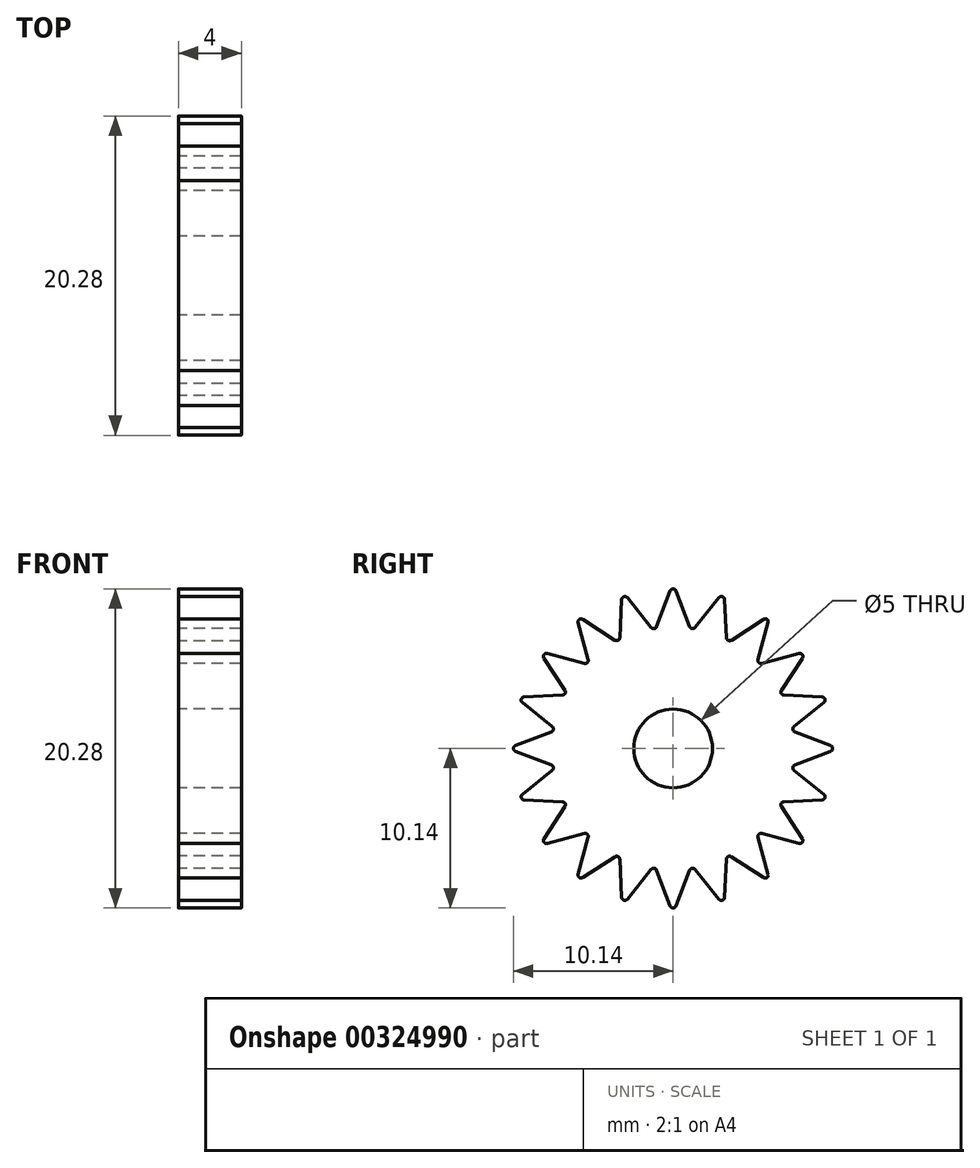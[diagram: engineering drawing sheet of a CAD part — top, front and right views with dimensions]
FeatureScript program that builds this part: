
annotation { "Feature Type Name" : "Feature", "Feature Type Description" : "" }
export const myFeature = defineFeature(function(context is Context, id is Id, definition is map)
    precondition{}
    {
        {
            var Q0;
            Q0=qCreatedBy(makeId("Right.planeOp"),FACE);
            var sketch = newSketch(context, id + "F0", { "sketchPlane" : qUnion([Q0])});
            skCircle(sketch, "E0", {"center": v(0, 0) * mm, "radius": 7.5 * mm, "construction": true});
            skLineSegment(sketch, "E1", {"start": v(-0.19, 10) * mm, "end": v(-1.05, 7.73) * mm});
            skLineSegment(sketch, "E2.MirrorCS", {"start": v(0.19, 10) * mm, "end": v(1.05, 7.73) * mm});
            skPoint(sketch, "E3.visualSharp", {"position": v(0, 10.5) * mm});
            skArc(sketch, "E3.filletArc", {"start": v(0.19, 10) * mm, "mid": v(0, 10.14) * mm, "end": v(-0.19, 10) * mm});
            skLineSegment(sketch, "E4.1.0", {"start": v(-3.27, 9.46) * mm, "end": v(-3.39, 7.03) * mm});
            skLineSegment(sketch, "E4.1.1", {"start": v(-2.91, 9.58) * mm, "end": v(-1.4, 7.68) * mm});
            skPoint(sketch, "E4.1.2", {"position": v(-3.24, 9.99) * mm});
            skArc(sketch, "E4.1.3", {"start": v(-2.91, 9.58) * mm, "mid": v(-3.13, 9.64) * mm, "end": v(-3.27, 9.46) * mm});
            skLineSegment(sketch, "E4.2.0", {"start": v(-6.03, 7.99) * mm, "end": v(-5.4, 5.64) * mm});
            skLineSegment(sketch, "E4.2.1", {"start": v(-5.73, 8.2) * mm, "end": v(-3.7, 6.87) * mm});
            skPoint(sketch, "E4.2.2", {"position": v(-6.17, 8.5) * mm});
            skArc(sketch, "E4.2.3", {"start": v(-5.73, 8.2) * mm, "mid": v(-5.96, 8.2) * mm, "end": v(-6.03, 7.99) * mm});
            skLineSegment(sketch, "E4.3.0", {"start": v(-8.2, 5.73) * mm, "end": v(-6.87, 3.7) * mm});
            skLineSegment(sketch, "E4.3.1", {"start": v(-7.99, 6.03) * mm, "end": v(-5.64, 5.4) * mm});
            skPoint(sketch, "E4.3.2", {"position": v(-8.5, 6.17) * mm});
            skArc(sketch, "E4.3.3", {"start": v(-7.99, 6.03) * mm, "mid": v(-8.2, 5.96) * mm, "end": v(-8.2, 5.73) * mm});
            skLineSegment(sketch, "E4.4.0", {"start": v(-9.58, 2.91) * mm, "end": v(-7.68, 1.4) * mm});
            skLineSegment(sketch, "E4.4.1", {"start": v(-9.46, 3.27) * mm, "end": v(-7.03, 3.39) * mm});
            skPoint(sketch, "E4.4.2", {"position": v(-9.99, 3.24) * mm});
            skArc(sketch, "E4.4.3", {"start": v(-9.46, 3.27) * mm, "mid": v(-9.64, 3.13) * mm, "end": v(-9.58, 2.91) * mm});
            skLineSegment(sketch, "E4.5.0", {"start": v(-10, -0.19) * mm, "end": v(-7.73, -1.05) * mm});
            skLineSegment(sketch, "E4.5.1", {"start": v(-10, 0.19) * mm, "end": v(-7.73, 1.05) * mm});
            skPoint(sketch, "E4.5.2", {"position": v(-10.5, 0) * mm});
            skArc(sketch, "E4.5.3", {"start": v(-10, 0.19) * mm, "mid": v(-10.14, 0) * mm, "end": v(-10, -0.19) * mm});
            skLineSegment(sketch, "E4.6.0", {"start": v(-9.46, -3.27) * mm, "end": v(-7.03, -3.39) * mm});
            skLineSegment(sketch, "E4.6.1", {"start": v(-9.58, -2.91) * mm, "end": v(-7.68, -1.4) * mm});
            skPoint(sketch, "E4.6.2", {"position": v(-9.99, -3.24) * mm});
            skArc(sketch, "E4.6.3", {"start": v(-9.58, -2.91) * mm, "mid": v(-9.64, -3.13) * mm, "end": v(-9.46, -3.27) * mm});
            skLineSegment(sketch, "E4.7.0", {"start": v(-7.99, -6.03) * mm, "end": v(-5.64, -5.4) * mm});
            skLineSegment(sketch, "E4.7.1", {"start": v(-8.2, -5.73) * mm, "end": v(-6.87, -3.7) * mm});
            skPoint(sketch, "E4.7.2", {"position": v(-8.5, -6.17) * mm});
            skArc(sketch, "E4.7.3", {"start": v(-8.2, -5.73) * mm, "mid": v(-8.2, -5.96) * mm, "end": v(-7.99, -6.03) * mm});
            skLineSegment(sketch, "E4.8.0", {"start": v(-5.73, -8.2) * mm, "end": v(-3.7, -6.87) * mm});
            skLineSegment(sketch, "E4.8.1", {"start": v(-6.03, -7.99) * mm, "end": v(-5.4, -5.64) * mm});
            skPoint(sketch, "E4.8.2", {"position": v(-6.17, -8.5) * mm});
            skArc(sketch, "E4.8.3", {"start": v(-6.03, -7.99) * mm, "mid": v(-5.96, -8.2) * mm, "end": v(-5.73, -8.2) * mm});
            skLineSegment(sketch, "E4.9.0", {"start": v(-2.91, -9.58) * mm, "end": v(-1.4, -7.68) * mm});
            skLineSegment(sketch, "E4.9.1", {"start": v(-3.27, -9.46) * mm, "end": v(-3.39, -7.03) * mm});
            skPoint(sketch, "E4.9.2", {"position": v(-3.24, -9.99) * mm});
            skArc(sketch, "E4.9.3", {"start": v(-3.27, -9.46) * mm, "mid": v(-3.13, -9.64) * mm, "end": v(-2.91, -9.58) * mm});
            skLineSegment(sketch, "E4.10.0", {"start": v(0.19, -10) * mm, "end": v(1.05, -7.73) * mm});
            skLineSegment(sketch, "E4.10.1", {"start": v(-0.19, -10) * mm, "end": v(-1.05, -7.73) * mm});
            skPoint(sketch, "E4.10.2", {"position": v(0, -10.5) * mm});
            skArc(sketch, "E4.10.3", {"start": v(-0.19, -10) * mm, "mid": v(0, -10.14) * mm, "end": v(0.19, -10) * mm});
            skLineSegment(sketch, "E4.11.0", {"start": v(3.27, -9.46) * mm, "end": v(3.39, -7.03) * mm});
            skLineSegment(sketch, "E4.11.1", {"start": v(2.91, -9.58) * mm, "end": v(1.4, -7.68) * mm});
            skPoint(sketch, "E4.11.2", {"position": v(3.24, -9.99) * mm});
            skArc(sketch, "E4.11.3", {"start": v(2.91, -9.58) * mm, "mid": v(3.13, -9.64) * mm, "end": v(3.27, -9.46) * mm});
            skLineSegment(sketch, "E4.12.0", {"start": v(6.03, -7.99) * mm, "end": v(5.4, -5.64) * mm});
            skLineSegment(sketch, "E4.12.1", {"start": v(5.73, -8.2) * mm, "end": v(3.7, -6.87) * mm});
            skPoint(sketch, "E4.12.2", {"position": v(6.17, -8.5) * mm});
            skArc(sketch, "E4.12.3", {"start": v(5.73, -8.2) * mm, "mid": v(5.96, -8.2) * mm, "end": v(6.03, -7.99) * mm});
            skLineSegment(sketch, "E4.13.0", {"start": v(8.2, -5.73) * mm, "end": v(6.87, -3.7) * mm});
            skLineSegment(sketch, "E4.13.1", {"start": v(7.99, -6.03) * mm, "end": v(5.64, -5.4) * mm});
            skPoint(sketch, "E4.13.2", {"position": v(8.5, -6.17) * mm});
            skArc(sketch, "E4.13.3", {"start": v(7.99, -6.03) * mm, "mid": v(8.2, -5.96) * mm, "end": v(8.2, -5.73) * mm});
            skLineSegment(sketch, "E4.14.0", {"start": v(9.58, -2.91) * mm, "end": v(7.68, -1.4) * mm});
            skLineSegment(sketch, "E4.14.1", {"start": v(9.46, -3.27) * mm, "end": v(7.03, -3.39) * mm});
            skPoint(sketch, "E4.14.2", {"position": v(9.99, -3.24) * mm});
            skArc(sketch, "E4.14.3", {"start": v(9.46, -3.27) * mm, "mid": v(9.64, -3.13) * mm, "end": v(9.58, -2.91) * mm});
            skLineSegment(sketch, "E4.15.0", {"start": v(10, 0.19) * mm, "end": v(7.73, 1.05) * mm});
            skLineSegment(sketch, "E4.15.1", {"start": v(10, -0.19) * mm, "end": v(7.73, -1.05) * mm});
            skPoint(sketch, "E4.15.2", {"position": v(10.5, 0) * mm});
            skArc(sketch, "E4.15.3", {"start": v(10, -0.19) * mm, "mid": v(10.14, 0) * mm, "end": v(10, 0.19) * mm});
            skLineSegment(sketch, "E4.16.0", {"start": v(9.46, 3.27) * mm, "end": v(7.03, 3.39) * mm});
            skLineSegment(sketch, "E4.16.1", {"start": v(9.58, 2.91) * mm, "end": v(7.68, 1.4) * mm});
            skPoint(sketch, "E4.16.2", {"position": v(9.99, 3.24) * mm});
            skArc(sketch, "E4.16.3", {"start": v(9.58, 2.91) * mm, "mid": v(9.64, 3.13) * mm, "end": v(9.46, 3.27) * mm});
            skLineSegment(sketch, "E4.17.0", {"start": v(7.99, 6.03) * mm, "end": v(5.64, 5.4) * mm});
            skLineSegment(sketch, "E4.17.1", {"start": v(8.2, 5.73) * mm, "end": v(6.87, 3.7) * mm});
            skPoint(sketch, "E4.17.2", {"position": v(8.5, 6.17) * mm});
            skArc(sketch, "E4.17.3", {"start": v(8.2, 5.73) * mm, "mid": v(8.2, 5.96) * mm, "end": v(7.99, 6.03) * mm});
            skLineSegment(sketch, "E4.18.0", {"start": v(5.73, 8.2) * mm, "end": v(3.7, 6.87) * mm});
            skLineSegment(sketch, "E4.18.1", {"start": v(6.03, 7.99) * mm, "end": v(5.4, 5.64) * mm});
            skPoint(sketch, "E4.18.2", {"position": v(6.17, 8.5) * mm});
            skArc(sketch, "E4.18.3", {"start": v(6.03, 7.99) * mm, "mid": v(5.96, 8.2) * mm, "end": v(5.73, 8.2) * mm});
            skLineSegment(sketch, "E4.19.0", {"start": v(2.91, 9.58) * mm, "end": v(1.4, 7.68) * mm});
            skLineSegment(sketch, "E4.19.1", {"start": v(3.27, 9.46) * mm, "end": v(3.39, 7.03) * mm});
            skPoint(sketch, "E4.19.2", {"position": v(3.24, 9.99) * mm});
            skArc(sketch, "E4.19.3", {"start": v(3.27, 9.46) * mm, "mid": v(3.13, 9.64) * mm, "end": v(2.91, 9.58) * mm});
            skPoint(sketch, "E5.visualSharp", {"position": v(1.17, 7.4) * mm});
            skArc(sketch, "E5.filletArc", {"start": v(1.05, 7.73) * mm, "mid": v(1.2, 7.6) * mm, "end": v(1.4, 7.68) * mm});
            skPoint(sketch, "E6.visualSharp", {"position": v(3.4, 6.68) * mm});
            skArc(sketch, "E6.filletArc", {"start": v(3.39, 7.03) * mm, "mid": v(3.5, 6.86) * mm, "end": v(3.7, 6.87) * mm});
            skPoint(sketch, "E7.visualSharp", {"position": v(5.3, 5.3) * mm});
            skArc(sketch, "E7.filletArc", {"start": v(5.4, 5.64) * mm, "mid": v(5.45, 5.45) * mm, "end": v(5.64, 5.4) * mm});
            skPoint(sketch, "E8.visualSharp", {"position": v(6.68, 3.4) * mm});
            skArc(sketch, "E8.filletArc", {"start": v(6.87, 3.7) * mm, "mid": v(6.86, 3.5) * mm, "end": v(7.03, 3.39) * mm});
            skPoint(sketch, "E9.visualSharp", {"position": v(7.4, 1.17) * mm});
            skArc(sketch, "E9.filletArc", {"start": v(7.68, 1.4) * mm, "mid": v(7.6, 1.2) * mm, "end": v(7.73, 1.05) * mm});
            skPoint(sketch, "E10.visualSharp", {"position": v(7.4, -1.17) * mm});
            skArc(sketch, "E10.filletArc", {"start": v(7.73, -1.05) * mm, "mid": v(7.6, -1.2) * mm, "end": v(7.68, -1.4) * mm});
            skPoint(sketch, "E11.visualSharp", {"position": v(-1.17, 7.4) * mm});
            skArc(sketch, "E11.filletArc", {"start": v(-1.4, 7.68) * mm, "mid": v(-1.2, 7.6) * mm, "end": v(-1.05, 7.73) * mm});
            skPoint(sketch, "E12.visualSharp", {"position": v(-3.4, 6.68) * mm});
            skArc(sketch, "E12.filletArc", {"start": v(-3.7, 6.87) * mm, "mid": v(-3.5, 6.86) * mm, "end": v(-3.39, 7.03) * mm});
            skPoint(sketch, "E13.visualSharp", {"position": v(-5.3, 5.3) * mm});
            skArc(sketch, "E13.filletArc", {"start": v(-5.64, 5.4) * mm, "mid": v(-5.45, 5.45) * mm, "end": v(-5.4, 5.64) * mm});
            skPoint(sketch, "E14.visualSharp", {"position": v(-6.68, 3.4) * mm});
            skArc(sketch, "E14.filletArc", {"start": v(-7.03, 3.39) * mm, "mid": v(-6.86, 3.5) * mm, "end": v(-6.87, 3.7) * mm});
            skPoint(sketch, "E15.visualSharp", {"position": v(-7.4, 1.17) * mm});
            skArc(sketch, "E15.filletArc", {"start": v(-7.73, 1.05) * mm, "mid": v(-7.6, 1.2) * mm, "end": v(-7.68, 1.4) * mm});
            skPoint(sketch, "E16.visualSharp", {"position": v(-7.4, -1.17) * mm});
            skArc(sketch, "E16.filletArc", {"start": v(-7.68, -1.4) * mm, "mid": v(-7.6, -1.2) * mm, "end": v(-7.73, -1.05) * mm});
            skPoint(sketch, "E17.visualSharp", {"position": v(-6.68, -3.4) * mm});
            skArc(sketch, "E17.filletArc", {"start": v(-6.87, -3.7) * mm, "mid": v(-6.86, -3.5) * mm, "end": v(-7.03, -3.39) * mm});
            skPoint(sketch, "E18.visualSharp", {"position": v(-5.3, -5.3) * mm});
            skArc(sketch, "E18.filletArc", {"start": v(-5.4, -5.64) * mm, "mid": v(-5.45, -5.45) * mm, "end": v(-5.64, -5.4) * mm});
            skPoint(sketch, "E19.visualSharp", {"position": v(-3.4, -6.68) * mm});
            skArc(sketch, "E19.filletArc", {"start": v(-3.39, -7.03) * mm, "mid": v(-3.5, -6.86) * mm, "end": v(-3.7, -6.87) * mm});
            skPoint(sketch, "E20.visualSharp", {"position": v(-1.17, -7.4) * mm});
            skArc(sketch, "E20.filletArc", {"start": v(-1.05, -7.73) * mm, "mid": v(-1.2, -7.6) * mm, "end": v(-1.4, -7.68) * mm});
            skPoint(sketch, "E21.visualSharp", {"position": v(1.17, -7.4) * mm});
            skArc(sketch, "E21.filletArc", {"start": v(1.4, -7.68) * mm, "mid": v(1.2, -7.6) * mm, "end": v(1.05, -7.73) * mm});
            skPoint(sketch, "E22.visualSharp", {"position": v(3.4, -6.68) * mm});
            skArc(sketch, "E22.filletArc", {"start": v(3.7, -6.87) * mm, "mid": v(3.5, -6.86) * mm, "end": v(3.39, -7.03) * mm});
            skPoint(sketch, "E23.visualSharp", {"position": v(5.3, -5.3) * mm});
            skArc(sketch, "E23.filletArc", {"start": v(5.64, -5.4) * mm, "mid": v(5.45, -5.45) * mm, "end": v(5.4, -5.64) * mm});
            skPoint(sketch, "E24.visualSharp", {"position": v(6.68, -3.4) * mm});
            skArc(sketch, "E24.filletArc", {"start": v(7.03, -3.39) * mm, "mid": v(6.86, -3.5) * mm, "end": v(6.87, -3.7) * mm});
            skSolve(sketch);
        }
        {
            var Q0;
            Q0=makeQuery(id+"F0.imprint","IMPRINT",FACE,{"disambiguationData":[TD([[makeQuery(id+"F0.imprint","IMPRINT",EDGE,{"derivedFrom":sQuery(id+"F0.wireOp",EDGE,"E1")}),1.0]])]});
            extrude(context, id + "F1", {"entities" : qUnion([Q0]), "depth" : 4 * mm});
        }
        {
            var Q0;
            Q0=qCreatedBy(makeId("Right.planeOp"),FACE);
            var sketch = newSketch(context, id + "F2", { "sketchPlane" : qUnion([Q0])});
            skCircle(sketch, "E25", {"center": v(0, 0) * mm, "radius": 2.5 * mm});
            skSolve(sketch);
        }
        {
            var Q0;
            Q0 = qSketchRegion(id + "F2", true);
            extrude(context, id + "F3", {"entities" : qUnion([Q0]), "operationType" : NewBodyOperationType.REMOVE, "endBound" : BoundingType.THROUGH_ALL, "depth" : 25 * mm});
        }
    });
